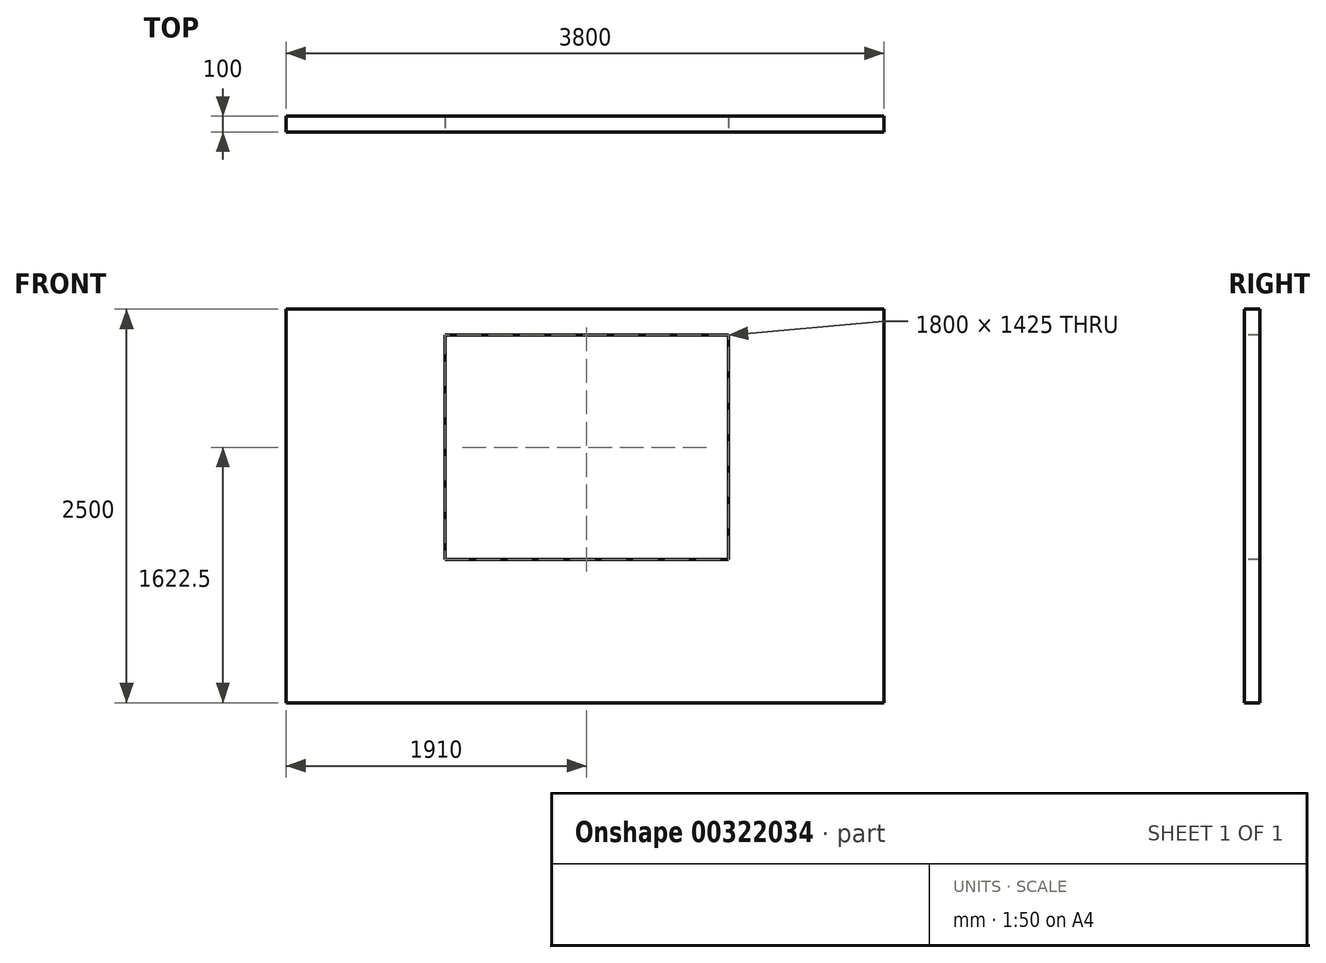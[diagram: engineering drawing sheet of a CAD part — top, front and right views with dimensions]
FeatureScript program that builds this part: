
annotation { "Feature Type Name" : "Feature", "Feature Type Description" : "" }
export const myFeature = defineFeature(function(context is Context, id is Id, definition is map)
    precondition{}
    {
        {
            var Q0;
            Q0=qCreatedBy(makeId("Front.planeOp"),FACE);
            var sketch = newSketch(context, id + "F0", { "sketchPlane" : qUnion([Q0])});
            skLineSegment(sketch, "E0.bottom", {"start": v(1900, 1250) * mm, "end": v(-1900, 1250) * mm});
            skLineSegment(sketch, "E0.top", {"start": v(1900, -1250) * mm, "end": v(-1900, -1250) * mm});
            skLineSegment(sketch, "E0.left", {"start": v(1900, 1250) * mm, "end": v(1900, -1250) * mm});
            skLineSegment(sketch, "E0.right", {"start": v(-1900, 1250) * mm, "end": v(-1900, -1250) * mm});
            skPoint(sketch, "E0.middle", {"position": v(0, 0) * mm});
            skSolve(sketch);
        }
        {
            var Q0;
            Q0=qSketchRegion(id+"F0",true);
            extrude(context, id + "F1", {"entities" : qUnion([Q0]), "depth" : 100 * mm});
        }
        {
            var Q0;
            Q0=makeQuery(id+"F1.opExtrude","CAP_FACE",FACE,{"disambiguationData":[OSD([sQuery(id+"F0.wireOp",EDGE,"E0.bottom"),sQuery(id+"F0.wireOp",EDGE,"E0.top"),sQuery(id+"F0.wireOp",EDGE,"E0.left"),sQuery(id+"F0.wireOp",EDGE,"E0.right")])],"isStart":false});
            var sketch = newSketch(context, id + "F2", { "sketchPlane" : qUnion([Q0])});
            skLineSegment(sketch, "E1.bottom", {"start": v(-890, 1085) * mm, "end": v(910, 1085) * mm});
            skLineSegment(sketch, "E1.top", {"start": v(-890, -340) * mm, "end": v(910, -340) * mm});
            skLineSegment(sketch, "E1.left", {"start": v(-890, 1085) * mm, "end": v(-890, -340) * mm});
            skLineSegment(sketch, "E1.right", {"start": v(910, 1085) * mm, "end": v(910, -340) * mm});
            skSolve(sketch);
        }
        {
            var Q0;
            Q0 = qSketchRegion(id + "F2", true);
            extrude(context, id + "F3", {"entities" : qUnion([Q0]), "operationType" : NewBodyOperationType.REMOVE, "endBound" : BoundingType.UP_TO_NEXT, "oppositeDirection" : true, "depth" : 25 * mm});
        }
    });
